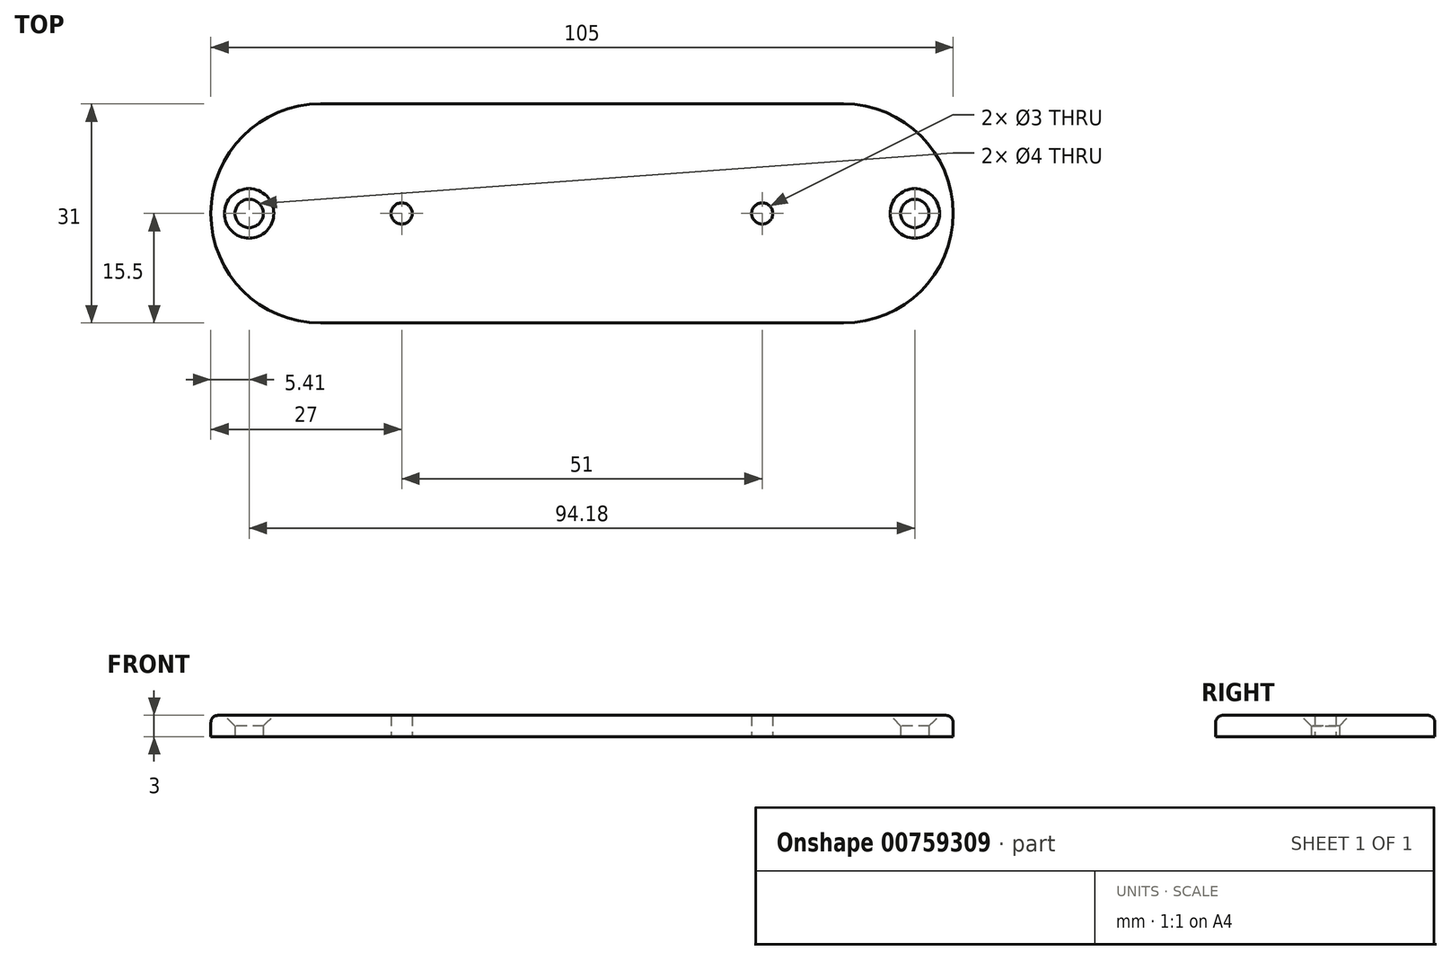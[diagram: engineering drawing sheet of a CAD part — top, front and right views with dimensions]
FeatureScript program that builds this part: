
annotation { "Feature Type Name" : "Feature", "Feature Type Description" : "" }
export const myFeature = defineFeature(function(context is Context, id is Id, definition is map)
    precondition{}
    {
        {
            var Q0;
            Q0=qCreatedBy(makeId("Top.planeOp"),FACE);
            var sketch = newSketch(context, id + "F0", { "sketchPlane" : qUnion([Q0])});
            skLineSegment(sketch, "E0.bottom", {"start": v(37, -15.5) * mm, "end": v(-37, -15.5) * mm});
            skLineSegment(sketch, "E0.top", {"start": v(37, 15.5) * mm, "end": v(-37, 15.5) * mm});
            skPoint(sketch, "E0.middle", {"position": v(0, 0) * mm});
            skArc(sketch, "E1", {"start": v(37, -15.5) * mm, "mid": v(52.5, 0) * mm, "end": v(37, 15.5) * mm});
            skArc(sketch, "E2", {"start": v(-37, 15.5) * mm, "mid": v(-52.5, 0) * mm, "end": v(-37, -15.5) * mm});
            skCircle(sketch, "E3", {"center": v(-25.5, 0) * mm, "radius": 1.5 * mm});
            skCircle(sketch, "E4", {"center": v(-47.1, 0) * mm, "radius": 2 * mm});
            skArc(sketch, "E5.MirrorCS", {"start": v(37, 15.5) * mm, "mid": v(52.5, 0) * mm, "end": v(37, -15.5) * mm});
            skCircle(sketch, "E6.MirrorC", {"center": v(47.1, 0) * mm, "radius": 2 * mm});
            skCircle(sketch, "E7.MirrorC", {"center": v(25.5, 0) * mm, "radius": 1.5 * mm});
            skPoint(sketch, "E8.start.orphan", {"position": v(-52.5, 0) * mm});
            skSolve(sketch);
        }
        {
            var Q0;
            Q0 = qSketchRegion(id + "F0", true);
            extrude(context, id + "F1", {"entities" : qUnion([Q0]), "depth" : 3 * mm, "offsetDistance" : 25 * mm});
        }
        {
            var Q0;
            Q0=makeQuery(id+"F1.opExtrude","CAP_EDGE",EDGE,{"disambiguationData":[OSD([sQuery(id+"F0.wireOp",EDGE,"E6.MirrorC")])],"isStart":false});
            var Q1;
            Q1=makeQuery(id+"F1.opExtrude","CAP_EDGE",EDGE,{"disambiguationData":[OSD([sQuery(id+"F0.wireOp",EDGE,"E4")])],"isStart":false});
            chamfer(context, id + "F2", {"entities" : qUnion([Q0, Q1]), "width" : 1.5 * mm, "tangentPropagation" : true});
        }
        {
            var Q0;
            Q0=makeQuery(id+"F1.opExtrude","CAP_EDGE",EDGE,{"disambiguationData":[OSD([sQuery(id+"F0.wireOp",EDGE,"E0.top")])],"isStart":false});
            var Q1;
            Q1=makeQuery(id+"F1.opExtrude","CAP_EDGE",EDGE,{"disambiguationData":[OSD([sQuery(id+"F0.wireOp",EDGE,"E2")])],"isStart":false});
            var Q2;
            Q2=makeQuery(id+"F1.opExtrude","CAP_EDGE",EDGE,{"disambiguationData":[OSD([sQuery(id+"F0.wireOp",EDGE,"E0.bottom")])],"isStart":false});
            var Q3;
            Q3=makeQuery(id+"F1.opExtrude","CAP_EDGE",EDGE,{"disambiguationData":[OSD([sQuery(id+"F0.wireOp",EDGE,"E5.MirrorCS")])],"isStart":false});
            fillet(context, id + "F3", {"entities" : qUnion([Q0, Q1, Q2, Q3]), "radius" : 1 * mm, "tangentPropagation" : true, "allowEdgeOverflow" : false});
        }
    });
